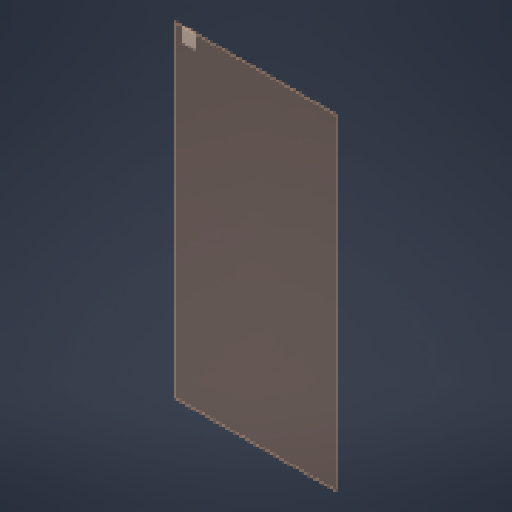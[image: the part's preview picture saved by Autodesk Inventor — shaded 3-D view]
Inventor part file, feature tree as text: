
AUTODESK INVENTOR PART (.ipt)
format: ipt  version: 2024 (Build 280153000, 153)  size: 126,464 bytes
history: native  units: mm
features: other x5, plane x1, extrude x1, sketch x1
ambient origin geometry x8: Origin, YZ Plane, XZ Plane, XY Plane, X Axis, Y Axis, Z Axis, Center Point
bodies: Body1 (feature_tree)
feature tree (8):
  other  "Sólido1"
  plane  "Plano de trabajo1"
  extrude  "Extrusión1"  Depth=30.0mm
  sketch  "Boceto1"  dims[d0=120.0mm d1=30.0mm d2=30.0mm d3=30.0mm d4=30.0mm d5=2.0mm d6=0.0mm]
  other  "<userpath>\Downloads\Piezas CMR\Marco_APM_003\Marco_apm_003-2.iam"
  other  "Marco_apm_003-2.iam"
  other  "Marco_Conveyor_Aereo:1"
  other  "Marco:1"
